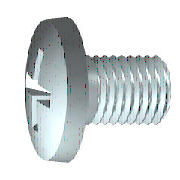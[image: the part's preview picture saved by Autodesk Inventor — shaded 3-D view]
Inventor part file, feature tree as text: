
AUTODESK INVENTOR PART (.ipt)
format: ipt  version: 2021 (Build 250183000, 183)  size: 249,344 bytes
history: native  units: mm (DEFAULTED — no unit token found)
features: chamfer x4, other x3, sketch x2, revolve x1, fillet x1, extrude x1, pattern_circular x1
ambient origin geometry x8: Origin, YZ Plane, XZ Plane, XY Plane, X Axis, Y Axis, Z Axis, Center Point
bodies: Solid1 (feature_tree)
feature tree (13):
  revolve  "Revolution1"  [1 undecoded]
  chamfer  "Chamfer1"  Distance=0.125mm
  chamfer  "Chamfer2"  Distance=0.125mm
  fillet  "Fillet1"  Radius=0.25mm
  extrude  "Extrusion1"  Depth=10.0mm
  pattern_circular  "PolarArray1"  [2 undecoded]
  chamfer  "Chamfer3"  Distance=1.612mm
  chamfer  "Chamfer4"  Distance=0.62mm
  other  "MSC_A1"
  other  "MSC_PF1"
  other  "MSC_PT1"
  sketch  "Sketch2"  dims[d6=2.75mm d9=0.872665mm]
  sketch  "Sketch3"  dims[d10=90.0deg d11=0.125mm d12=0.125mm d13=0.25mm d14=0.25mm d16=10.0mm d17=0.0mm d19=1.612mm d20=0.62mm d21=2.52mm d22=0.516667mm d23=0.0mm d24=40.0mm d26=360.0deg d28=0.0mm d29=0.0mm d30=0.442857mm d31=0.442857mm d32=0.206667mm d33=0.206667mm d34=45.0deg d35=45.0deg d36=45.0deg d37=45.0deg d38=0.0mm d39=0.0mm d40=0.0mm]
note: 3 required parameter values undecoded (feature->parameter linkage not recoverable at this tier; creation-order binding heuristic only, values carry confidence <= 0.55)